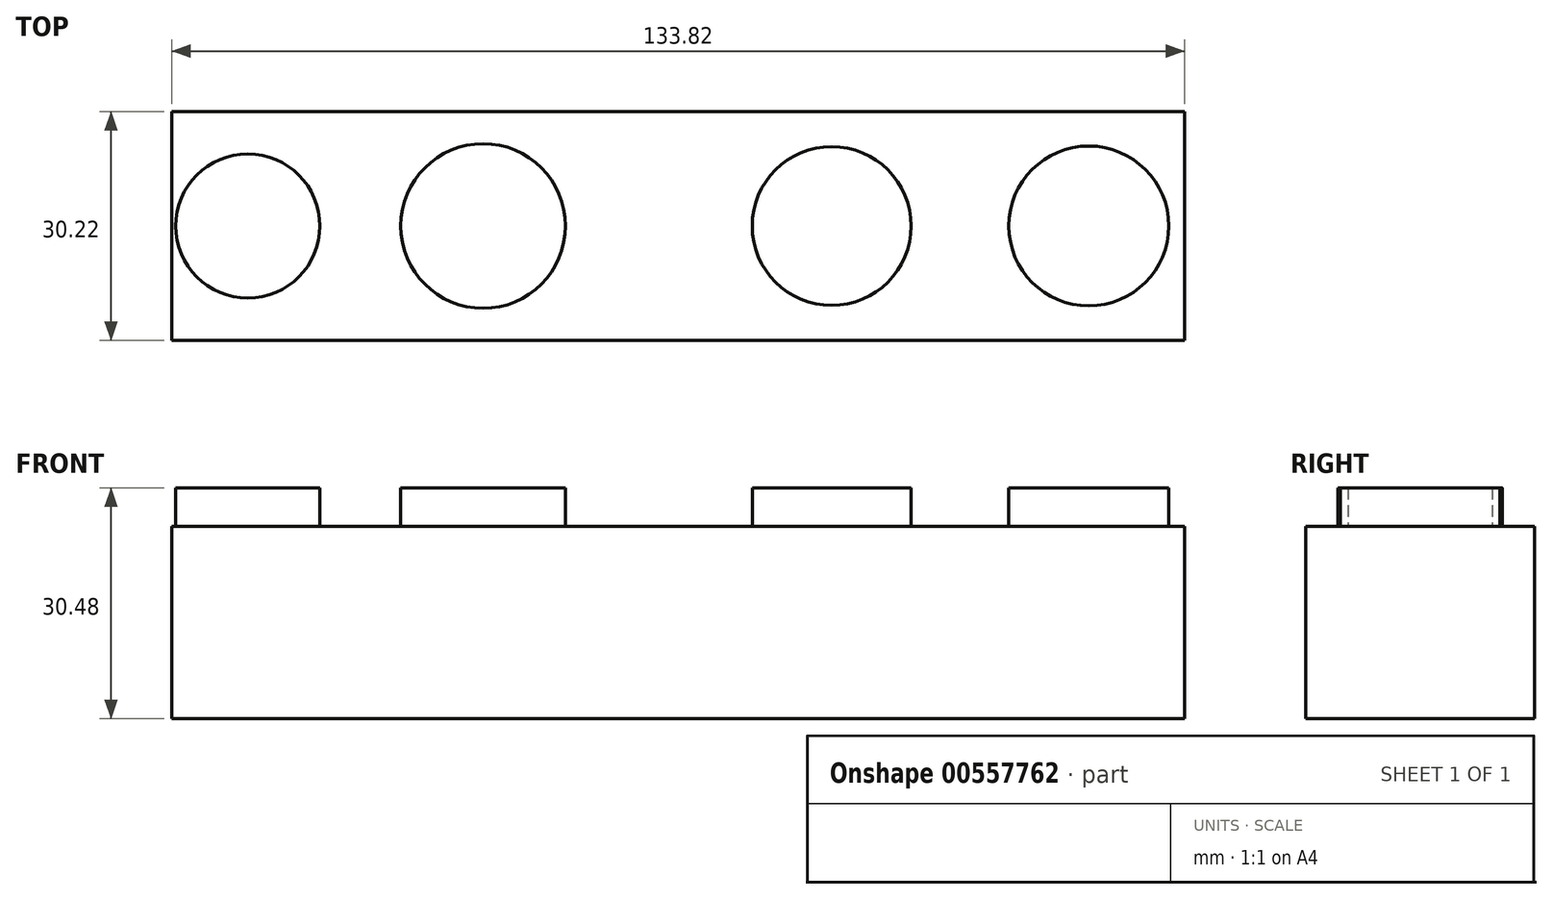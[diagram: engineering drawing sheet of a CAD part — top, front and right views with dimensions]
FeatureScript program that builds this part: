
annotation { "Feature Type Name" : "Feature", "Feature Type Description" : "" }
export const myFeature = defineFeature(function(context is Context, id is Id, definition is map)
    precondition{}
    {
        {
            var Q0;
            Q0=qCreatedBy(makeId("Top.planeOp"),FACE);
            var sketch = newSketch(context, id + "F0", { "sketchPlane" : qUnion([Q0])});
            skLineSegment(sketch, "E0.bottom", {"start": v(66.91, 15.1) * mm, "end": v(-66.91, 15.1) * mm});
            skLineSegment(sketch, "E0.top", {"start": v(66.91, -15.1) * mm, "end": v(-66.91, -15.1) * mm});
            skLineSegment(sketch, "E0.left", {"start": v(66.91, 15.1) * mm, "end": v(66.91, -15.1) * mm});
            skLineSegment(sketch, "E0.right", {"start": v(-66.91, 15.1) * mm, "end": v(-66.91, -15.1) * mm});
            skPoint(sketch, "E0.middle", {"position": v(0, 0) * mm});
            skCircle(sketch, "E1", {"center": v(-49.65, 0) * mm, "radius": 12.68 * mm});
            skCircle(sketch, "E2", {"center": v(0, 0) * mm, "radius": 13.13 * mm});
            skCircle(sketch, "E3", {"center": v(45.04, 0) * mm, "radius": 13.21 * mm});
            skSolve(sketch);
        }
        {
            var Q0;
            Q0=makeQuery(id+"F0.imprint","IMPRINT",FACE,{"disambiguationData":[TD([[makeQuery(id+"F0.imprint","IMPRINT",EDGE,{"derivedFrom":sQuery(id+"F0.wireOp",EDGE,"E1")}),1.0]])]});
            var Q1;
            Q1=makeQuery(id+"F0.imprint","IMPRINT",FACE,{"disambiguationData":[TD([[makeQuery(id+"F0.imprint","IMPRINT",EDGE,{"derivedFrom":sQuery(id+"F0.wireOp",EDGE,"E0.bottom")}),1.0]])]});
            var Q2;
            Q2=makeQuery(id+"F0.imprint","IMPRINT",FACE,{"disambiguationData":[TD([[makeQuery(id+"F0.imprint","IMPRINT",EDGE,{"derivedFrom":sQuery(id+"F0.wireOp",EDGE,"E2")}),1.0]])]});
            var Q3;
            Q3=makeQuery(id+"F0.imprint","IMPRINT",FACE,{"disambiguationData":[TD([[makeQuery(id+"F0.imprint","IMPRINT",EDGE,{"derivedFrom":sQuery(id+"F0.wireOp",EDGE,"E3")}),1.0]])]});
            extrude(context, id + "F1", {"entities" : qUnion([Q0, Q1, Q2, Q3]), "depth" : 25.4 * mm, "offsetDistance" : 25.4 * mm});
        }
        {
            var Q0;
            Q0=makeQuery(id+"F1.opExtrude","CAP_FACE",FACE,{"disambiguationData":[OSD([sQuery(id+"F0.wireOp",EDGE,"E0.bottom"),sQuery(id+"F0.wireOp",EDGE,"E0.top"),sQuery(id+"F0.wireOp",EDGE,"E0.left"),sQuery(id+"F0.wireOp",EDGE,"E0.right")])],"isStart":true});
            var sketch = newSketch(context, id + "F2", { "sketchPlane" : qUnion([Q0])});
            skCircle(sketch, "E4", {"center": v(-56.84, 0) * mm, "radius": 9.53 * mm});
            skCircle(sketch, "E5", {"center": v(-25.76, 0) * mm, "radius": 10.88 * mm});
            skCircle(sketch, "E6", {"center": v(20.3, 0) * mm, "radius": 10.5 * mm});
            skCircle(sketch, "E7", {"center": v(54.25, 0) * mm, "radius": 10.56 * mm});
            skSolve(sketch);
        }
        {
            var Q0;
            Q0=makeQuery(id+"F2.imprint","IMPRINT",FACE,{"disambiguationData":[TD([[makeQuery(id+"F2.imprint","IMPRINT",EDGE,{"derivedFrom":sQuery(id+"F2.wireOp",EDGE,"E4")}),1.0]])]});
            var Q1;
            Q1=makeQuery(id+"F2.imprint","IMPRINT",FACE,{"disambiguationData":[TD([[makeQuery(id+"F2.imprint","IMPRINT",EDGE,{"derivedFrom":sQuery(id+"F2.wireOp",EDGE,"E5")}),1.0]])]});
            var Q2;
            Q2=makeQuery(id+"F2.imprint","IMPRINT",FACE,{"disambiguationData":[TD([[makeQuery(id+"F2.imprint","IMPRINT",EDGE,{"derivedFrom":sQuery(id+"F2.wireOp",EDGE,"E6")}),1.0]])]});
            var Q3;
            Q3=makeQuery(id+"F2.imprint","IMPRINT",FACE,{"disambiguationData":[TD([[makeQuery(id+"F2.imprint","IMPRINT",EDGE,{"derivedFrom":sQuery(id+"F2.wireOp",EDGE,"E7")}),1.0]])]});
            extrude(context, id + "F3", {"entities" : qUnion([Q0, Q1, Q2, Q3]), "operationType" : NewBodyOperationType.ADD, "oppositeDirection" : true, "depth" : 30.48 * mm, "offsetDistance" : 25.4 * mm});
        }
    });
